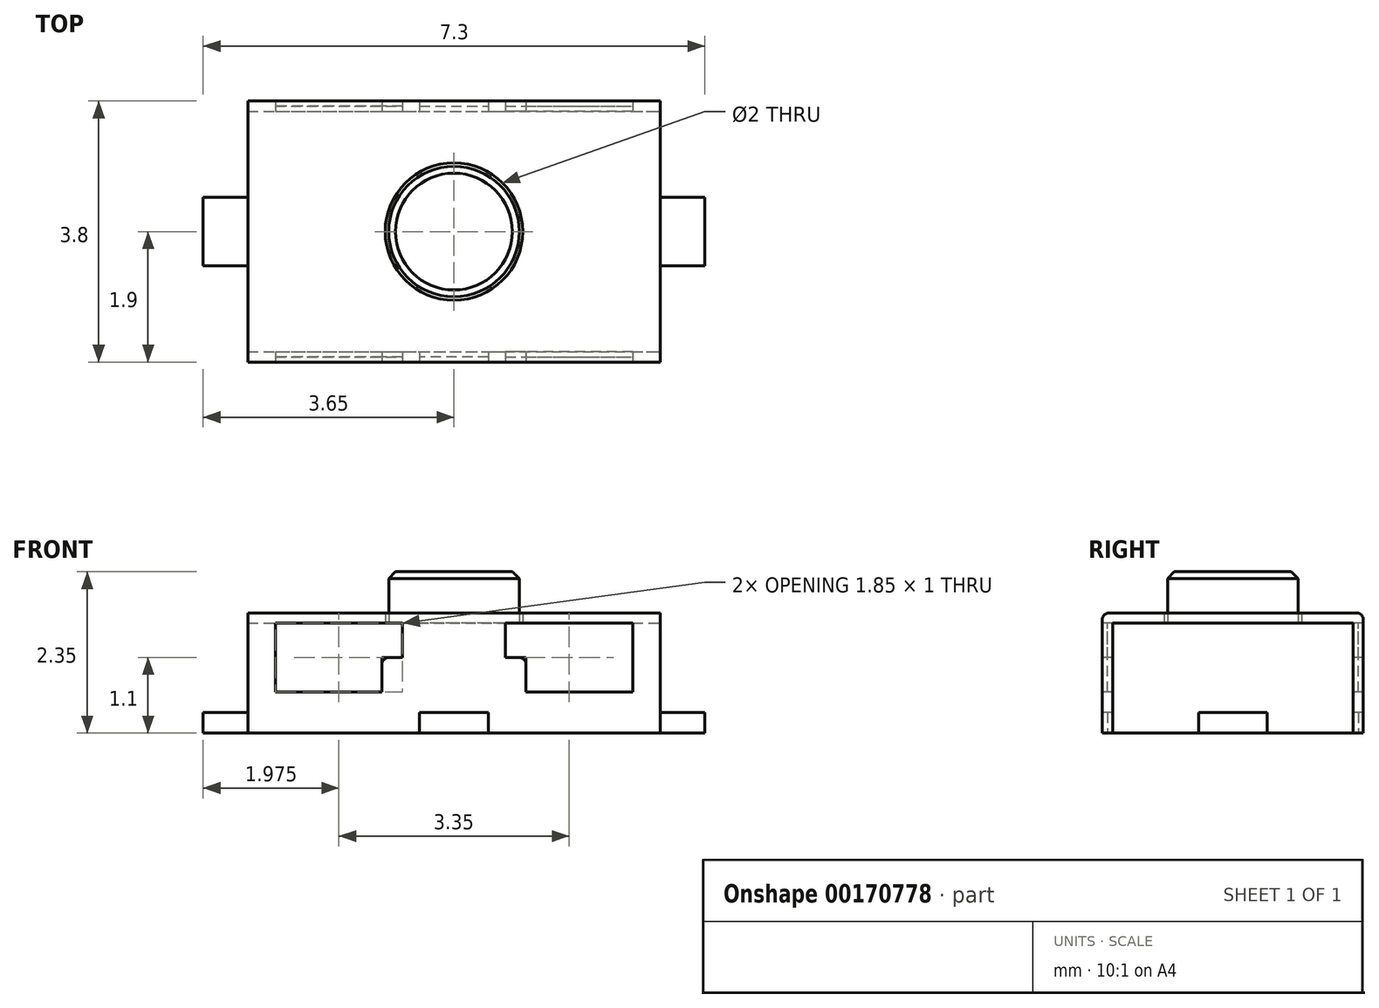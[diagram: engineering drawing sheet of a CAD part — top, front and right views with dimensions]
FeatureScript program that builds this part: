
annotation { "Feature Type Name" : "Feature", "Feature Type Description" : "" }
export const myFeature = defineFeature(function(context is Context, id is Id, definition is map)
    precondition{}
    {
        {
            var Q0;
            Q0=qCreatedBy(makeId("Top.planeOp"),FACE);
            var sketch = newSketch(context, id + "F0", { "sketchPlane" : qUnion([Q0])});
            skLineSegment(sketch, "E0.bottom", {"start": v(-3, 1.9) * mm, "end": v(3, 1.9) * mm});
            skLineSegment(sketch, "E0.top", {"start": v(-3, -1.9) * mm, "end": v(3, -1.9) * mm});
            skLineSegment(sketch, "E0.left", {"start": v(-3, 1.9) * mm, "end": v(-3, -1.9) * mm});
            skLineSegment(sketch, "E0.right", {"start": v(3, 1.9) * mm, "end": v(3, -1.9) * mm});
            skLineSegment(sketch, "E1", {"start": v(-3, 1.9) * mm, "end": v(3, -1.9) * mm, "construction": true});
            skLineSegment(sketch, "E2", {"start": v(-3, 0.5) * mm, "end": v(-3.65, 0.5) * mm});
            skLineSegment(sketch, "E3", {"start": v(-3.65, 0.5) * mm, "end": v(-3.65, -0.5) * mm});
            skLineSegment(sketch, "E4", {"start": v(-3.65, -0.5) * mm, "end": v(-3, -0.5) * mm});
            skLineSegment(sketch, "E5.MirrorCS", {"start": v(3.65, -0.5) * mm, "end": v(3, -0.5) * mm});
            skLineSegment(sketch, "E6.MirrorCS", {"start": v(3, 0.5) * mm, "end": v(3.65, 0.5) * mm});
            skLineSegment(sketch, "E7.MirrorCS", {"start": v(3.65, 0.5) * mm, "end": v(3.65, -0.5) * mm});
            skCircle(sketch, "E8", {"center": v(0, 0) * mm, "radius": 1 * mm});
            skSolve(sketch);
        }
        {
            var Q0;
            {var subQ3=sQuery(id+"F0.wireOp",EDGE,"E0.bottom");Q0=makeQuery(id+"F0.imprint","IMPRINT",FACE,{"disambiguationData":[TD([[makeQuery(id+"F0.imprint","IMPRINT",EDGE,{"derivedFrom":subQ3}),-1.0]])]});}
            extrude(context, id + "F1", {"entities" : qUnion([Q0]), "depth" : 1.75 * mm, "offsetDistance" : 25 * mm});
        }
        {
            var Q0;
            {var subQ0=sQuery(id+"F0.wireOp",EDGE,"E2");Q0=makeQuery(id+"F0.imprint","IMPRINT",FACE,{"disambiguationData":[TD([[makeQuery(id+"F0.imprint","IMPRINT",EDGE,{"derivedFrom":subQ0}),1.0]])]});}
            var Q1;
            {var subQ0=sQuery(id+"F0.wireOp",EDGE,"E5.MirrorCS");Q1=makeQuery(id+"F0.imprint","IMPRINT",FACE,{"disambiguationData":[TD([[makeQuery(id+"F0.imprint","IMPRINT",EDGE,{"derivedFrom":subQ0}),-1.0]])]});}
            extrude(context, id + "F2", {"entities" : qUnion([Q0, Q1]), "operationType" : NewBodyOperationType.ADD, "depth" : 0.3 * mm, "offsetDistance" : 25 * mm});
        }
        {
            var Q0;
            Q0=qCreatedBy(makeId("Front.planeOp"),FACE);
            var sketch = newSketch(context, id + "F3", { "sketchPlane" : qUnion([Q0])});
            skLineSegment(sketch, "E9.bottom", {"start": v(-2.6, 1.6) * mm, "end": v(-0.75, 1.6) * mm});
            skLineSegment(sketch, "E9.top", {"start": v(-2.6, 1.1) * mm, "end": v(-0.75, 1.1) * mm});
            skLineSegment(sketch, "E9.left", {"start": v(-2.6, 1.6) * mm, "end": v(-2.6, 1.1) * mm});
            skLineSegment(sketch, "E9.right", {"start": v(-0.75, 1.6) * mm, "end": v(-0.75, 1.1) * mm});
            skLineSegment(sketch, "E10.bottom", {"start": v(-2.6, 1.1) * mm, "end": v(-1.05, 1.1) * mm});
            skLineSegment(sketch, "E10.top", {"start": v(-2.6, 0.6) * mm, "end": v(-1.05, 0.6) * mm});
            skLineSegment(sketch, "E10.left", {"start": v(-2.6, 1.1) * mm, "end": v(-2.6, 0.6) * mm});
            skLineSegment(sketch, "E10.right", {"start": v(-1.05, 1.1) * mm, "end": v(-1.05, 0.6) * mm});
            skLineSegment(sketch, "E11.MirrorCS", {"start": v(2.6, 1.1) * mm, "end": v(1.05, 1.1) * mm});
            skLineSegment(sketch, "E12.MirrorCS", {"start": v(2.6, 1.6) * mm, "end": v(0.75, 1.6) * mm});
            skLineSegment(sketch, "E13.MirrorCS", {"start": v(2.6, 0.6) * mm, "end": v(1.05, 0.6) * mm});
            skLineSegment(sketch, "E14.MirrorCS", {"start": v(0.75, 1.6) * mm, "end": v(0.75, 1.1) * mm});
            skLineSegment(sketch, "E15.MirrorCS", {"start": v(1.05, 1.1) * mm, "end": v(1.05, 0.6) * mm});
            skLineSegment(sketch, "E16.MirrorCS", {"start": v(2.6, 1.1) * mm, "end": v(2.6, 0.6) * mm});
            skLineSegment(sketch, "E17.MirrorCS", {"start": v(2.6, 1.1) * mm, "end": v(0.75, 1.1) * mm});
            skLineSegment(sketch, "E18.MirrorCS", {"start": v(2.6, 1.6) * mm, "end": v(2.6, 1.1) * mm});
            skLineSegment(sketch, "E19.bottom", {"start": v(-0.5, 0) * mm, "end": v(0.5, 0) * mm});
            skLineSegment(sketch, "E19.top", {"start": v(-0.5, 0.3) * mm, "end": v(0.5, 0.3) * mm});
            skLineSegment(sketch, "E19.left", {"start": v(-0.5, 0) * mm, "end": v(-0.5, 0.3) * mm});
            skLineSegment(sketch, "E19.right", {"start": v(0.5, 0) * mm, "end": v(0.5, 0.3) * mm});
            skSolve(sketch);
        }
        {
            var Q0;
            Q0 = qSketchRegion(id + "F3", true);
            extrude(context, id + "F4", {"entities" : qUnion([Q0]), "operationType" : NewBodyOperationType.REMOVE, "endBound" : BoundingType.THROUGH_ALL, "oppositeDirection" : true, "depth" : 25 * mm, "offsetDistance" : 25 * mm, "hasSecondDirection" : true, "secondDirectionBound" : BoundingType.THROUGH_ALL, "secondDirectionOppositeDirection" : false, "secondDirectionDepth" : 25 * mm});
        }
        {
            var Q0;
            {var subQ0=sQuery(id+"F0.wireOp",EDGE,"E8");var subQ1=sQuery(id+"F0.wireOp",EDGE,"E0.left");var subQ2=sQuery(id+"F0.wireOp",EDGE,"E0.top");var subQ3=sQuery(id+"F0.wireOp",EDGE,"E0.bottom");var subQ4=sQuery(id+"F0.wireOp",EDGE,"E3");var subQ5=sQuery(id+"F0.wireOp",EDGE,"E2");var subQ6=sQuery(id+"F0.wireOp",EDGE,"E4");var subQ7=sQuery(id+"F0.wireOp",EDGE,"E0.right");Q0=makeQuery(id+"F4.boolean.opBoolean","SPLIT",FACE,{"disambiguationData":[TD([makeQuery(id+"F1.opExtrude","SWEPT_FACE",FACE,{"disambiguationData":[OSD([subQ1])]})])],"derivedFrom":makeQuery(id+"F2.boolean.opBoolean","MERGE",FACE,{"derivedFrom":[makeQuery(id+"F1.opExtrude","CAP_FACE",FACE,{"disambiguationData":[OSD([subQ3,subQ2,subQ1,subQ7,subQ0])],"isStart":true}),makeQuery(id+"F2.opExtrude","CAP_FACE",FACE,{"disambiguationData":[OSD([subQ1,subQ5,subQ4,subQ6])],"isStart":true}),makeQuery(id+"F2.opExtrude","CAP_FACE",FACE,{"disambiguationData":[OSD([subQ7,sQuery(id+"F0.wireOp",EDGE,"E5.MirrorCS"),sQuery(id+"F0.wireOp",EDGE,"E6.MirrorCS"),sQuery(id+"F0.wireOp",EDGE,"E7.MirrorCS")])],"isStart":true})]})});}
            var sketch = newSketch(context, id + "F5", { "sketchPlane" : qUnion([Q0])});
            skLineSegment(sketch, "E20.bottom", {"start": v(-3, -1.75) * mm, "end": v(3, -1.75) * mm});
            skLineSegment(sketch, "E20.top", {"start": v(-3, 1.75) * mm, "end": v(3, 1.75) * mm});
            skLineSegment(sketch, "E20.left", {"start": v(-3, -1.75) * mm, "end": v(-3, 1.75) * mm});
            skLineSegment(sketch, "E20.right", {"start": v(3, -1.75) * mm, "end": v(3, 1.75) * mm});
            skSolve(sketch);
        }
        {
            var Q0;
            Q0 = qSketchRegion(id + "F5", true);
            extrude(context, id + "F6", {"entities" : qUnion([Q0]), "operationType" : NewBodyOperationType.REMOVE, "oppositeDirection" : true, "depth" : 1.6 * mm, "offsetDistance" : 25 * mm});
        }
        {
            var Q0;
            {var subQ0=sQuery(id+"F0.wireOp",EDGE,"E0.top");var subQ1=makeQuery(id+"F1.opExtrude","SWEPT_FACE",FACE,{"disambiguationData":[OSD([subQ0])]});var subQ2=sQuery(id+"F0.wireOp",EDGE,"E4");var subQ3=sQuery(id+"F0.wireOp",EDGE,"E3");var subQ4=sQuery(id+"F0.wireOp",EDGE,"E2");var subQ5=sQuery(id+"F0.wireOp",EDGE,"E0.left");var subQ6=makeQuery(id+"F2.opExtrude","CAP_FACE",FACE,{"disambiguationData":[OSD([subQ5,subQ4,subQ3,subQ2])],"isStart":true});var subQ7=sQuery(id+"F0.wireOp",EDGE,"E8");var subQ9=sQuery(id+"F0.wireOp",EDGE,"E0.right");var subQ10=sQuery(id+"F0.wireOp",EDGE,"E0.bottom");var subQ11=makeQuery(id+"F1.opExtrude","CAP_FACE",FACE,{"disambiguationData":[OSD([subQ10,subQ0,subQ5,subQ9,subQ7])],"isStart":true});var subQ12=makeQuery(id+"F2.opExtrude","CAP_FACE",FACE,{"disambiguationData":[OSD([subQ9,sQuery(id+"F0.wireOp",EDGE,"E5.MirrorCS"),sQuery(id+"F0.wireOp",EDGE,"E6.MirrorCS"),sQuery(id+"F0.wireOp",EDGE,"E7.MirrorCS")])],"isStart":true});var subQ14=makeQuery(id+"F1.opExtrude","SWEPT_FACE",FACE,{"disambiguationData":[OSD([subQ5])]});Q0=makeQuery(id+"F6.boolean.opBoolean","SPLIT",FACE,{"disambiguationData":[TD([subQ1])],"derivedFrom":makeQuery(id+"F4.boolean.opBoolean","SPLIT",FACE,{"disambiguationData":[TD([subQ14])],"derivedFrom":makeQuery(id+"F2.boolean.opBoolean","MERGE",FACE,{"derivedFrom":[subQ11,subQ6,subQ12]})})});}
            var sketch = newSketch(context, id + "F7", { "sketchPlane" : qUnion([Q0])});
            skLineSegment(sketch, "E21.bottom", {"start": v(-3, 1.83) * mm, "end": v(3, 1.83) * mm});
            skLineSegment(sketch, "E21.top", {"start": v(-3, -1.83) * mm, "end": v(3, -1.83) * mm});
            skLineSegment(sketch, "E21.left", {"start": v(-3, 1.83) * mm, "end": v(-3, -1.83) * mm});
            skLineSegment(sketch, "E21.right", {"start": v(3, 1.83) * mm, "end": v(3, -1.83) * mm});
            skSolve(sketch);
        }
        {
            var Q0;
            Q0 = qSketchRegion(id + "F7", true);
            extrude(context, id + "F8", {"entities" : qUnion([Q0]), "oppositeDirection" : true, "depth" : 1.6 * mm, "offsetDistance" : 25 * mm});
        }
        {
            var Q0;
            Q0=makeQuery(id+"F6.boolean.opBoolean","SPLIT",BODY,{"disambiguationData":[OD(2.0)],"derivedFrom":makeQuery(id+"F1.opExtrude","SWEPT_BODY",BODY,{"disambiguationData":[OSD([sQuery(id+"F0.wireOp",EDGE,"E0.bottom"),sQuery(id+"F0.wireOp",EDGE,"E0.top"),sQuery(id+"F0.wireOp",EDGE,"E0.left"),sQuery(id+"F0.wireOp",EDGE,"E0.right"),sQuery(id+"F0.wireOp",EDGE,"E8")])]})});
            var Q1;
            Q1=makeQuery(id+"F8.opExtrude","SWEPT_BODY",BODY,{"disambiguationData":[OSD([sQuery(id+"F7.wireOp",EDGE,"E21.bottom"),sQuery(id+"F7.wireOp",EDGE,"E21.top"),sQuery(id+"F7.wireOp",EDGE,"E21.left"),sQuery(id+"F7.wireOp",EDGE,"E21.right")])]});
            booleanBodies(context, id + "F9", {"operationType" : BooleanOperationType.SUBTRACTION, "tools" : qUnion([Q0]), "targets" : qUnion([Q1]), "keepTools" : true});
        }
        {
            var Q0;
            Q0=makeQuery(id+"F8.opExtrude","CAP_FACE",FACE,{"disambiguationData":[OSD([sQuery(id+"F7.wireOp",EDGE,"E21.bottom"),sQuery(id+"F7.wireOp",EDGE,"E21.top"),sQuery(id+"F7.wireOp",EDGE,"E21.left"),sQuery(id+"F7.wireOp",EDGE,"E21.right")])],"isStart":false});
            var sketch = newSketch(context, id + "F10", { "sketchPlane" : qUnion([Q0])});
            skCircle(sketch, "E22", {"center": v(0, 0) * mm, "radius": 0.95 * mm});
            skSolve(sketch);
        }
        {
            var Q0;
            Q0 = qSketchRegion(id + "F10", true);
            extrude(context, id + "F11", {"entities" : qUnion([Q0]), "operationType" : NewBodyOperationType.ADD, "depth" : (2.5 - 1.75) * mm, "offsetDistance" : 25 * mm});
        }
        {
            var Q0;
            Q0=makeQuery(id+"F1.opExtrude","CAP_EDGE",EDGE,{"disambiguationData":[OSD([sQuery(id+"F0.wireOp",EDGE,"E0.top")])],"isStart":false});
            var Q1;
            Q1=makeQuery(id+"F1.opExtrude","CAP_EDGE",EDGE,{"disambiguationData":[OSD([sQuery(id+"F0.wireOp",EDGE,"E0.bottom")])],"isStart":false});
            var Q2;
            {var subQ0=sQuery(id+"F3.wireOp",EDGE,"E9.top");var subQ1=sQuery(id+"F3.wireOp",EDGE,"E10.right");Q2=makeQuery(id+"F6.boolean.opBoolean","SPLIT",EDGE,{"disambiguationData":[TD([makeQuery(id+"F1.opExtrude","SWEPT_FACE",FACE,{"disambiguationData":[OSD([sQuery(id+"F0.wireOp",EDGE,"E0.top")])]})])],"derivedFrom":makeQuery(id+"F4.boolean.opBoolean","COPY",EDGE,{"derivedFrom":makeQuery(id+"F4.opExtrude","SWEPT_EDGE",EDGE,{"disambiguationData":[OSD([subQ0,sQuery(id+"F3.wireOp",EDGE,"E10.bottom"),subQ1])]})})});}
            var Q3;
            {var subQ0=sQuery(id+"F3.wireOp",EDGE,"E15.MirrorCS");var subQ1=sQuery(id+"F3.wireOp",EDGE,"E17.MirrorCS");Q3=makeQuery(id+"F6.boolean.opBoolean","SPLIT",EDGE,{"disambiguationData":[TD([makeQuery(id+"F1.opExtrude","SWEPT_FACE",FACE,{"disambiguationData":[OSD([sQuery(id+"F0.wireOp",EDGE,"E0.top")])]})])],"derivedFrom":makeQuery(id+"F4.boolean.opBoolean","COPY",EDGE,{"derivedFrom":makeQuery(id+"F4.opExtrude","SWEPT_EDGE",EDGE,{"disambiguationData":[OSD([subQ0,subQ1])]})})});}
            var Q4;
            {var subQ0=sQuery(id+"F3.wireOp",EDGE,"E10.right");var subQ1=sQuery(id+"F3.wireOp",EDGE,"E9.top");Q4=makeQuery(id+"F6.boolean.opBoolean","SPLIT",EDGE,{"disambiguationData":[TD([makeQuery(id+"F1.opExtrude","SWEPT_FACE",FACE,{"disambiguationData":[OSD([sQuery(id+"F0.wireOp",EDGE,"E0.bottom")])]})])],"derivedFrom":makeQuery(id+"F4.boolean.opBoolean","COPY",EDGE,{"derivedFrom":makeQuery(id+"F4.opExtrude","SWEPT_EDGE",EDGE,{"disambiguationData":[OSD([subQ1,sQuery(id+"F3.wireOp",EDGE,"E10.bottom"),subQ0])]})})});}
            var Q5;
            {var subQ0=sQuery(id+"F3.wireOp",EDGE,"E17.MirrorCS");var subQ1=sQuery(id+"F3.wireOp",EDGE,"E15.MirrorCS");Q5=makeQuery(id+"F6.boolean.opBoolean","SPLIT",EDGE,{"disambiguationData":[TD([makeQuery(id+"F1.opExtrude","SWEPT_FACE",FACE,{"disambiguationData":[OSD([sQuery(id+"F0.wireOp",EDGE,"E0.bottom")])]})])],"derivedFrom":makeQuery(id+"F4.boolean.opBoolean","COPY",EDGE,{"derivedFrom":makeQuery(id+"F4.opExtrude","SWEPT_EDGE",EDGE,{"disambiguationData":[OSD([subQ1,subQ0])]})})});}
            fillet(context, id + "F12", {"entities" : qUnion([Q0, Q1, Q2, Q3, Q4, Q5]), "radius" : 0.1 * mm, "tangentPropagation" : true, "allowEdgeOverflow" : false});
        }
        {
            var Q0;
            Q0=makeQuery(id+"F11.opExtrude","CAP_FACE",FACE,{"disambiguationData":[OSD([sQuery(id+"F10.wireOp",EDGE,"E22")])],"isStart":false});
            chamfer(context, id + "F13", {"entities" : qUnion([Q0]), "width" : 0.1 * mm, "tangentPropagation" : true});
        }
    });
